# Revit family: Titus CBAL2-24 Wide, Linear Chilled Beam, Face Hosted, Revit 2020, R1.2
name_source: partatom
category: Mechanical Equipment
units: mm (PartAtom-declared; Revit-internal decimal feet)

## family parameters
Cut with Voids When Loaded = Yes
Host = Face
OmniClass Number = 23.75.70.17.31
OmniClass Title = Induction Units
Part Type = Normal
Room Calculation Point = No
Round Connector Dimension = Use Radius
Shared = No

## types (2) — shared parameters
1/2" In MNPT = No
1/2" in Sweat = Yes
10 Feet = No
10" Oval = No
2 - Two-way,Throw = No
2 Feet = Yes
2-Pipe System = No
24" Wide Beam = Yes
26 - White = Yes
2P1C - 2 Pipe, 1 Coil Circuit = No
2P2C - 2 Pipe, 2 Coil Circuit = No
3 Feet = No
3/4" In MNPT = No
4 Feet = No
4" Dia. = No
4-Pipe System = Yes
4P1C - 4 Pipe, 1 Coil Circuit = Yes
4P2C - 4 Pipe, 2 Coil Circuit = No
5 Feet = No
5" Dia. = No
6 Feet = No
6" Dia. = No
7 Feet = No
8 Feet = No
8" Oval = Yes
84 - Black = No
9 Feet = No
Actual Cooling Entering Dry Bulb Temperature = 0 °F
Actual Cooling Entering Wet Bulb Temperature = 0 °F
Actual Cooling Leaving Dry Bulb Temperature = 0 °F
Actual Cooling Leaving Wet Bulb Temperature = 0 °F
Actual External Static Pressure = 0.00 in-wg
Actual Heating Entering Dry Bulb Temperature = 0 °F
Actual Heating Leaving Dry Bulb Temperature = 0 °F
Actual Height = 8 3/8"
Actual Oval Width = 9 3/8"
Actual Oval height = 5 1/4"
Actual Radius = 1 15/16"
Actual Total Static Pressure = 0.00 in-wg
B - One-way, Back = No
CTRL Angle = 90.00°
CTRL Multi-Inlet Angle = 90.00°
CTRL Multi-Inlet Offset = 0"
CTRL Multi-Inlet Oval Angle = 90.00°
CTRL Multi-Inlet Round Angle = 0.00°
CTRL Multi-Inlet Round Connector Offset = 6 5/64"
CTRL Oval Connector Offset = 0"
CTRL Perforation Hole Dia = 1/8"
CTRL Perforation Offset = 1/2"
CTRL Round Connector Offset = 4"
CTRL Thickness = 1/16"
CWR Outlet Description = CWR-Outlet
CWS Inlet Description = CWS Inlet
Coil Material = Metal - Copper
Condenser Inlet Radius = 1/4"
Condenser Outlet Radius = 1/4"
Condenser Pressure Drop = 0.00 psi
Conditioned Air (Oval) Description = Conditioned Air
Conditioned Air (Round) Description = Disabled
Conditioned Air Connection Height = 5 1/4"
Conditioned Air Connection Radius = 1/4"
Conditioned Air Connection Width = 9 3/8"
Connector Offset = 6 5/64"
Default Elevation = 0"
Description = Linear Chilled Beam Diffuser, Ceiling Mounted
Design Ambient Summer Dry Bulb Temperature = 0 °F
Design Ambient Winter Dry Bulb Temperature = 0 °F
Design Ambient summer Wet bulb Temperature = 0 °F
Design Cooling Minimum Air Flow = 0 CFM
Design Heating Maximum Air Flow = 0 CFM
Design Heating Minimum Air Flow = 0 CFM
Design cooling Maximum Air Flow = 0 CFM
Evaporator Inlet Radius = 1/4"
Evaporator Outlet Radius = 1/4"
Evaporator Pressure Drop = 0.00 psi
F = 4 1/2"
F - One-way, Front = Yes
Frame Extension = 3/8"
G = 4"
H12 - SS Flex Hose - 12in = No
H18 - SS Flex Hose - 18in = No
H24 - SS Flex Hose - 24in = No
HWR Description = HWR Outlet
HWS Inlet Description = HWS Inlet
Hanger Visibility = No
Height = 10 1/8"
Hor Chilled Water Return Offset = 7 1/8"
Hor Chilled Water Supply Offset = 7 3/4"
Hor Hot Water Return Offset = 2 1/2"
Hor Hot Water Supply Offset = 2 1/2"
Inner Width = 23 3/8"
Input your Special Finish's name = Input your Special Finish's name
Lay In Width = 23 3/4"
M13 = Yes
M17 = No
M19 = No
M23 = No
M27 = No
M31 = No
Manufacturer = Titus HVAC
Material = Galvanized G90
Model = CBAL2-24
Multi-Inlet = Yes
Pipe Connections Left Hand = No
Pipe Connections Right Hand = Yes
Pipe Height = 6"
Primary Air Extension = 2 5/8"
Primary Air Ver Offset = 6 1/8"
Select a Beam Length = 1
Select a Piping Connection Type = 1
Select a Water Coil Connection = 2
Select a Water-Coil Type = 2
Select an Air Inlet Dia = 3
Select an Air Inlet Location = 4
Select an Air Nozzle Configuration = 1
Select an Air Throw Pattern = 2
Select an Exposed Face Finish = 1
Show Oval Connector = Yes
Show Room Tag = No
Show Round Connector = No
Side Middle = No
Side Plate = Yes
Top Middle = No
Top Plate = Yes
zero-valued in all types: Actual Coefficient of Performance, Actual Energy Efficiency Rating (BTU/h.W), Actual Filter Face Area, Actual Full Load Efficiency

## per-type parameters (varying)
| type | 3 - LAY-IN | CTRL Multi-Inlet Connector Offset | CTRL Multi-Inlet Oval Connector Offset | CTRL Offset | CTRL Pipe Connector Offset | CWR Ver Offset | CWS Ver Offset | HWR Ver Offset | HWS Ver Offset | Hanger Dimension F | Inner Length | Layin depath | NT - Tegular 9/16 Inch | Select Border Type | Total Length | Total Width |
| CBAL2-24 LAY-IN | Yes | 8 7/8" | 8 7/8" | 0" | 22 5/64" | 7 1/8" | 7 7/8" | 9 5/8" | 10 3/8" | 4 1/2" | 23 3/8" | 5/16" | No | 1 | 23 3/4" | 23 3/4" |
| CBAL2-24 NT Border Type | No | 8 1/2" | 8 1/2" | 7/16" | 21 45/64" | 7" | 7 5/8" | 9 1/2" | 10 1/8" | 4 5/16" | 23" | 3/8" | Yes | 2 | 23 3/8" | 23 3/8" |

## geometry (parser evidence)
native form markers: Sweep x23
no freeform markers — native parametric forms only
